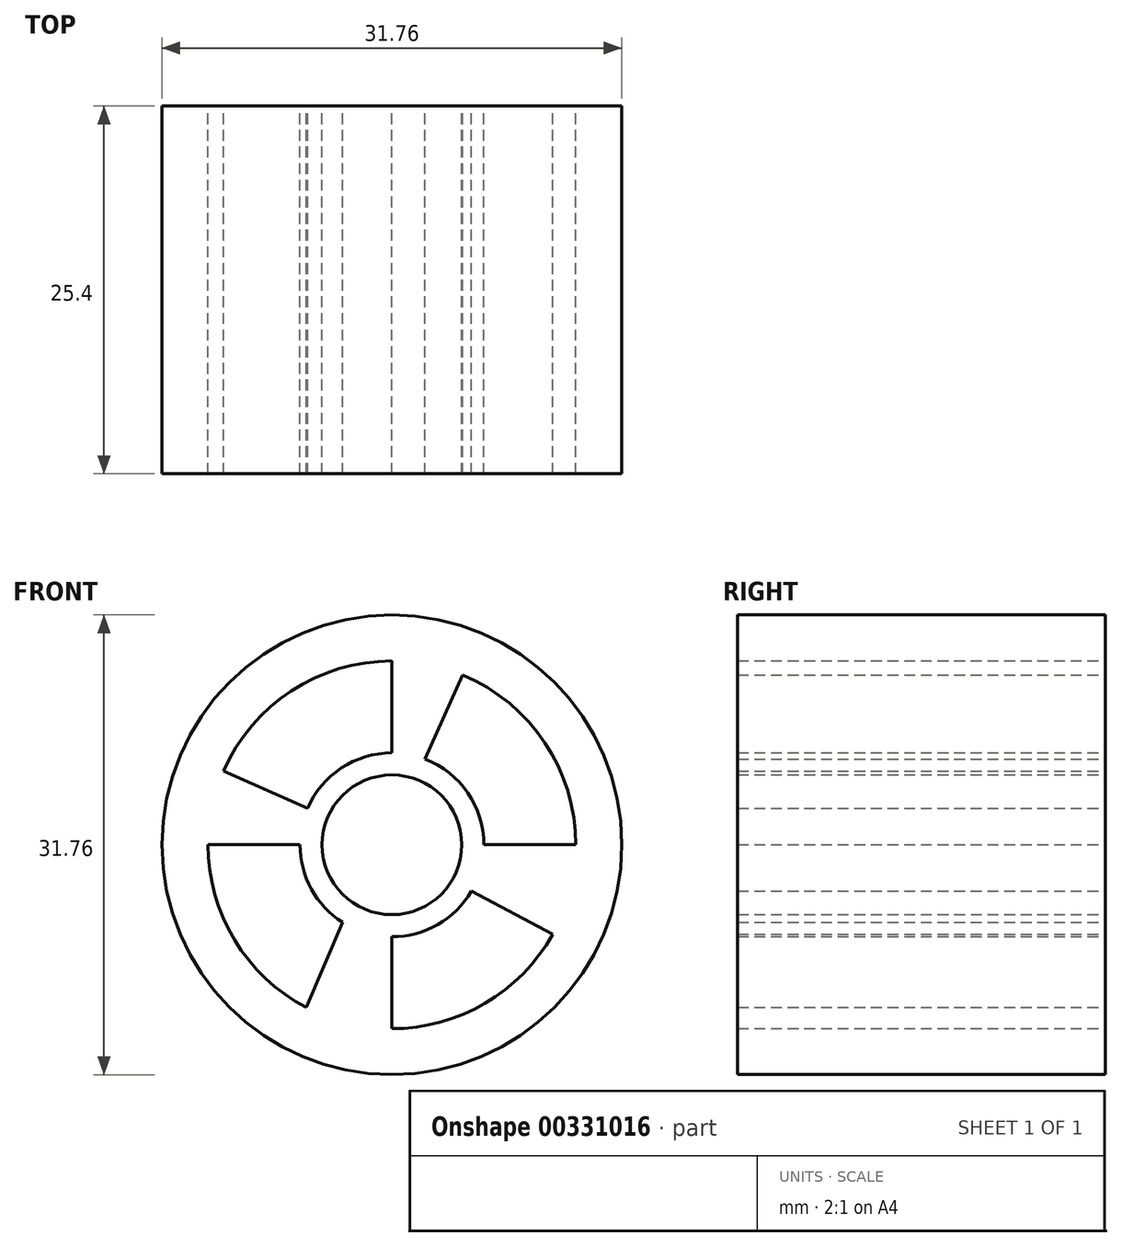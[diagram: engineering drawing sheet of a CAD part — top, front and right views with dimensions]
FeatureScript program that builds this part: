
annotation { "Feature Type Name" : "Feature", "Feature Type Description" : "" }
export const myFeature = defineFeature(function(context is Context, id is Id, definition is map)
    precondition{}
    {
        {
            var Q0;
            Q0=qCreatedBy(makeId("Front.planeOp"),FACE);
            var sketch = newSketch(context, id + "F0", { "sketchPlane" : qUnion([Q0])});
            skCircle(sketch, "E0", {"center": v(0, 0) * mm, "radius": 12.7 * mm});
            skCircle(sketch, "E1", {"center": v(0, 0) * mm, "radius": 6.35 * mm});
            skLineSegment(sketch, "E2", {"start": v(0, 6.35) * mm, "end": v(0, 12.7) * mm});
            skLineSegment(sketch, "E3", {"start": v(2.28, 5.93) * mm, "end": v(4.9, 11.72) * mm});
            skLineSegment(sketch, "E4", {"start": v(6.35, 0) * mm, "end": v(12.7, 0) * mm});
            skLineSegment(sketch, "E5", {"start": v(5.48, -3.2) * mm, "end": v(11.1, -6.19) * mm});
            skLineSegment(sketch, "E6", {"start": v(0, -6.35) * mm, "end": v(0, -12.7) * mm});
            skLineSegment(sketch, "E7", {"start": v(-3.42, -5.35) * mm, "end": v(-5.91, -11.24) * mm});
            skLineSegment(sketch, "E8", {"start": v(-6.35, 0) * mm, "end": v(-12.7, 0) * mm});
            skLineSegment(sketch, "E9", {"start": v(-5.83, 2.5) * mm, "end": v(-11.63, 5.1) * mm});
            skCircle(sketch, "E10", {"center": v(0, 0) * mm, "radius": 15.88 * mm});
            skCircle(sketch, "E11", {"center": v(0, 0) * mm, "radius": 4.83 * mm});
            skSolve(sketch);
        }
        {
            var Q0;
            Q0=qSketchRegion(id+"F0",true);
            var Q1;
            {var subQ0=sQuery(id+"F0.wireOp",EDGE,"E2");Q1=makeQuery(id+"F0.imprint","IMPRINT",FACE,{"disambiguationData":[TD([[makeQuery(id+"F0.imprint","IMPRINT",EDGE,{"derivedFrom":subQ0}),-1.0]])]});}
            var Q2;
            {var subQ0=sQuery(id+"F0.wireOp",EDGE,"E8");Q2=makeQuery(id+"F0.imprint","IMPRINT",FACE,{"disambiguationData":[TD([[makeQuery(id+"F0.imprint","IMPRINT",EDGE,{"derivedFrom":subQ0}),-1.0]])]});}
            var Q3;
            {var subQ0=sQuery(id+"F0.wireOp",EDGE,"E6");Q3=makeQuery(id+"F0.imprint","IMPRINT",FACE,{"disambiguationData":[TD([[makeQuery(id+"F0.imprint","IMPRINT",EDGE,{"derivedFrom":subQ0}),-1.0]])]});}
            var Q4;
            {var subQ0=sQuery(id+"F0.wireOp",EDGE,"E4");Q4=makeQuery(id+"F0.imprint","IMPRINT",FACE,{"disambiguationData":[TD([[makeQuery(id+"F0.imprint","IMPRINT",EDGE,{"derivedFrom":subQ0}),-1.0]])]});}
            var Q5;
            Q5=makeQuery(id+"F0.imprint","IMPRINT",FACE,{"disambiguationData":[TD([[makeQuery(id+"F0.imprint","IMPRINT",EDGE,{"derivedFrom":sQuery(id+"F0.wireOp",EDGE,"E11")}),-1.0]])]});
            extrude(context, id + "F1", {"entities" : qUnion([Q0, Q1, Q2, Q3, Q4, Q5]), "depth" : 25.4 * mm});
        }
    });
